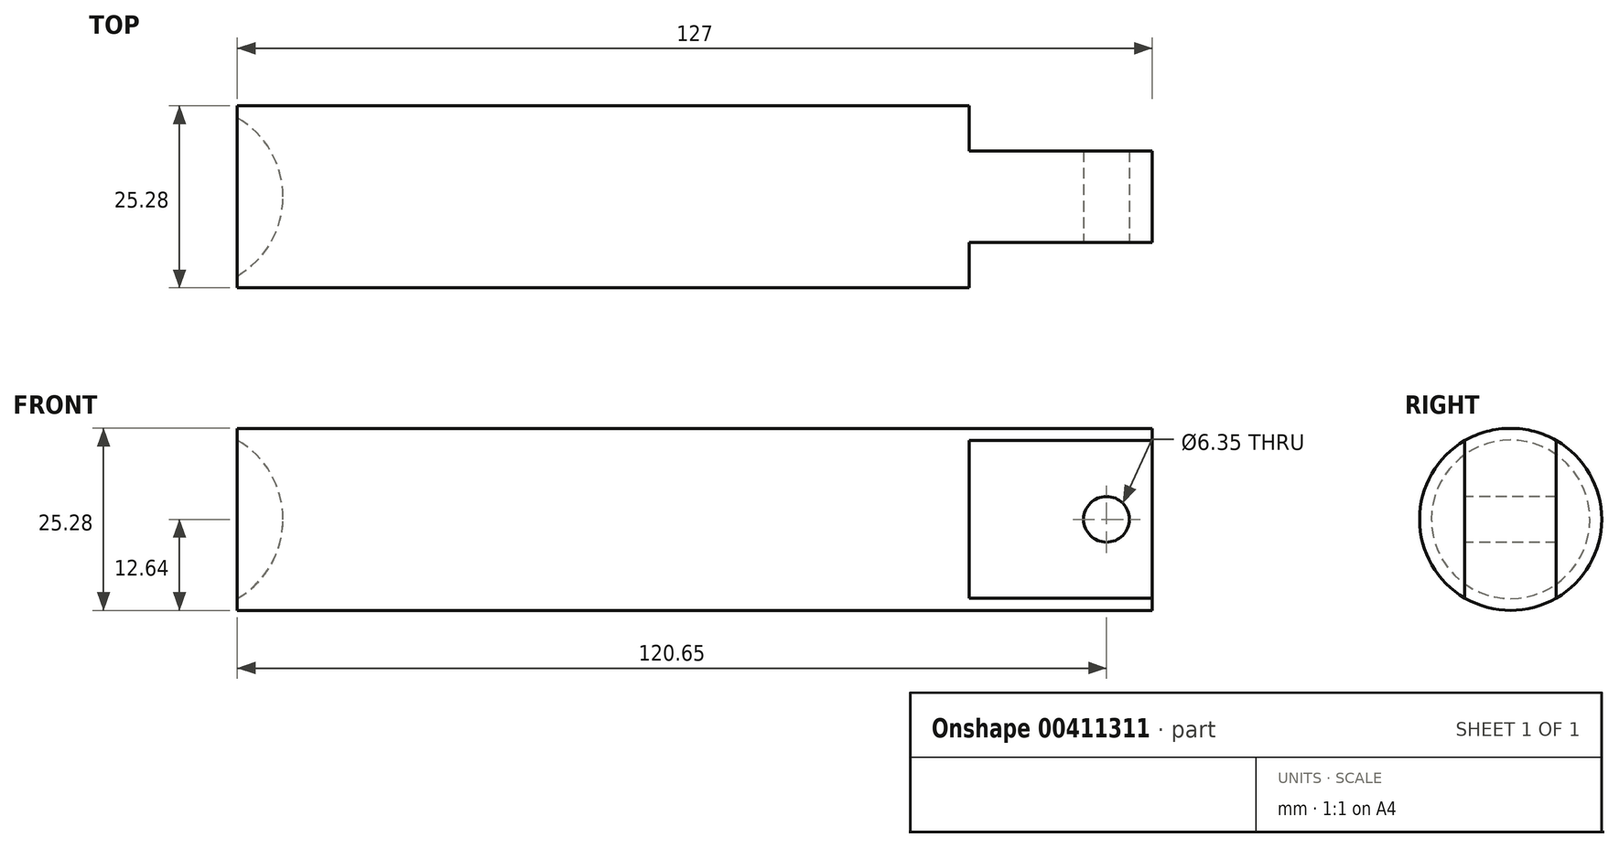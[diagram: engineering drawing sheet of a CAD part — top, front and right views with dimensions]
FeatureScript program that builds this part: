
annotation { "Feature Type Name" : "Feature", "Feature Type Description" : "" }
export const myFeature = defineFeature(function(context is Context, id is Id, definition is map)
    precondition{}
    {
        {
            var Q0;
            Q0=qCreatedBy(makeId("Front.planeOp"),FACE);
            var sketch = newSketch(context, id + "F0", { "sketchPlane" : qUnion([Q0])});
            skLineSegment(sketch, "E0.bottom", {"start": v(6.35, 0) * mm, "end": v(133.35, 0) * mm});
            skLineSegment(sketch, "E0.top", {"start": v(6.35, 12.64) * mm, "end": v(133.35, 12.64) * mm});
            skLineSegment(sketch, "E0.left", {"start": v(6.35, 0) * mm, "end": v(6.35, 12.64) * mm});
            skLineSegment(sketch, "E0.right", {"start": v(133.35, 0) * mm, "end": v(133.35, 12.64) * mm});
            skSolve(sketch);
        }
        {
            var Q0;
            Q0=makeQuery(id+"F0.imprint","IMPRINT",FACE,{"disambiguationData":[TD([[makeQuery(id+"F0.imprint","IMPRINT",EDGE,{"derivedFrom":sQuery(id+"F0.wireOp",EDGE,"E0.bottom")}),1.0]])]});
            var Q1;
            Q1=sQuery(id+"F0.wireOp",EDGE,"E0.bottom");
            revolve(context, id + "F1", {"entities" : qUnion([Q0]), "axis" : qUnion([Q1]), "revolveType" : RevolveType.FULL});
        }
        {
            var Q0;
            Q0=qCreatedBy(makeId("Front.planeOp"),FACE);
            var sketch = newSketch(context, id + "F2", { "sketchPlane" : qUnion([Q0])});
            skArc(sketch, "E1", {"start": v(12.7, 0) * mm, "mid": v(0, 12.7) * mm, "end": v(-12.7, 0) * mm});
            skLineSegment(sketch, "E2", {"start": v(-12.7, 0) * mm, "end": v(12.7, 0) * mm});
            skSolve(sketch);
        }
        {
            var Q0;
            Q0=makeQuery(id+"F2.imprint","IMPRINT",FACE,{"disambiguationData":[TD([[makeQuery(id+"F2.imprint","IMPRINT",EDGE,{"derivedFrom":sQuery(id+"F2.wireOp",EDGE,"E1")}),1.0]])]});
            var Q1;
            Q1=sQuery(id+"F2.wireOp",EDGE,"E2");
            revolve(context, id + "F3", {"operationType" : NewBodyOperationType.REMOVE, "entities" : qUnion([Q0]), "axis" : qUnion([Q1]), "revolveType" : RevolveType.FULL, "oppositeDirection" : true});
        }
        {
            var Q0;
            Q0=makeQuery(id+"F1.opRevolve","SWEPT_FACE",FACE,{"disambiguationData":[OSD([sQuery(id+"F0.wireOp",EDGE,"E0.right")])]});
            var sketch = newSketch(context, id + "F4", { "sketchPlane" : qUnion([Q0])});
            skLineSegment(sketch, "E3.bottom", {"start": v(-17.94, 23.57) * mm, "end": v(-6.35, 23.57) * mm});
            skLineSegment(sketch, "E3.top", {"start": v(-17.94, -22.55) * mm, "end": v(-6.35, -22.55) * mm});
            skLineSegment(sketch, "E3.left", {"start": v(-17.94, 23.57) * mm, "end": v(-17.94, -22.55) * mm});
            skLineSegment(sketch, "E3.right", {"start": v(-6.35, 23.57) * mm, "end": v(-6.35, -22.55) * mm});
            skLineSegment(sketch, "E4.bottom", {"start": v(19.72, 23.57) * mm, "end": v(6.35, 23.57) * mm});
            skLineSegment(sketch, "E4.top", {"start": v(19.72, -16.54) * mm, "end": v(6.35, -16.54) * mm});
            skLineSegment(sketch, "E4.left", {"start": v(19.72, 23.57) * mm, "end": v(19.72, -16.54) * mm});
            skLineSegment(sketch, "E4.right", {"start": v(6.35, 23.57) * mm, "end": v(6.35, -16.54) * mm});
            skSolve(sketch);
        }
        {
            var Q0;
            Q0 = qSketchRegion(id + "F4", true);
            extrude(context, id + "F5", {"entities" : qUnion([Q0]), "operationType" : NewBodyOperationType.REMOVE, "oppositeDirection" : true, "depth" : 25.4 * mm});
        }
        {
            var Q0;
            Q0=makeQuery(id+"F5.boolean.opBoolean","COPY",FACE,{"derivedFrom":makeQuery(id+"F5.opExtrude","SWEPT_FACE",FACE,{"disambiguationData":[OSD([sQuery(id+"F4.wireOp",EDGE,"E3.right")])]})});
            var sketch = newSketch(context, id + "F6", { "sketchPlane" : qUnion([Q0])});
            skCircle(sketch, "E5", {"center": v(127, 0) * mm, "radius": 3.18 * mm});
            skPoint(sketch, "E5.centerSnap0", {"position": v(133.35, 0) * mm});
            skSolve(sketch);
        }
        {
            var Q0;
            Q0 = qSketchRegion(id + "F6", true);
            extrude(context, id + "F7", {"entities" : qUnion([Q0]), "operationType" : NewBodyOperationType.REMOVE, "oppositeDirection" : true, "depth" : 25.4 * mm});
        }
    });
